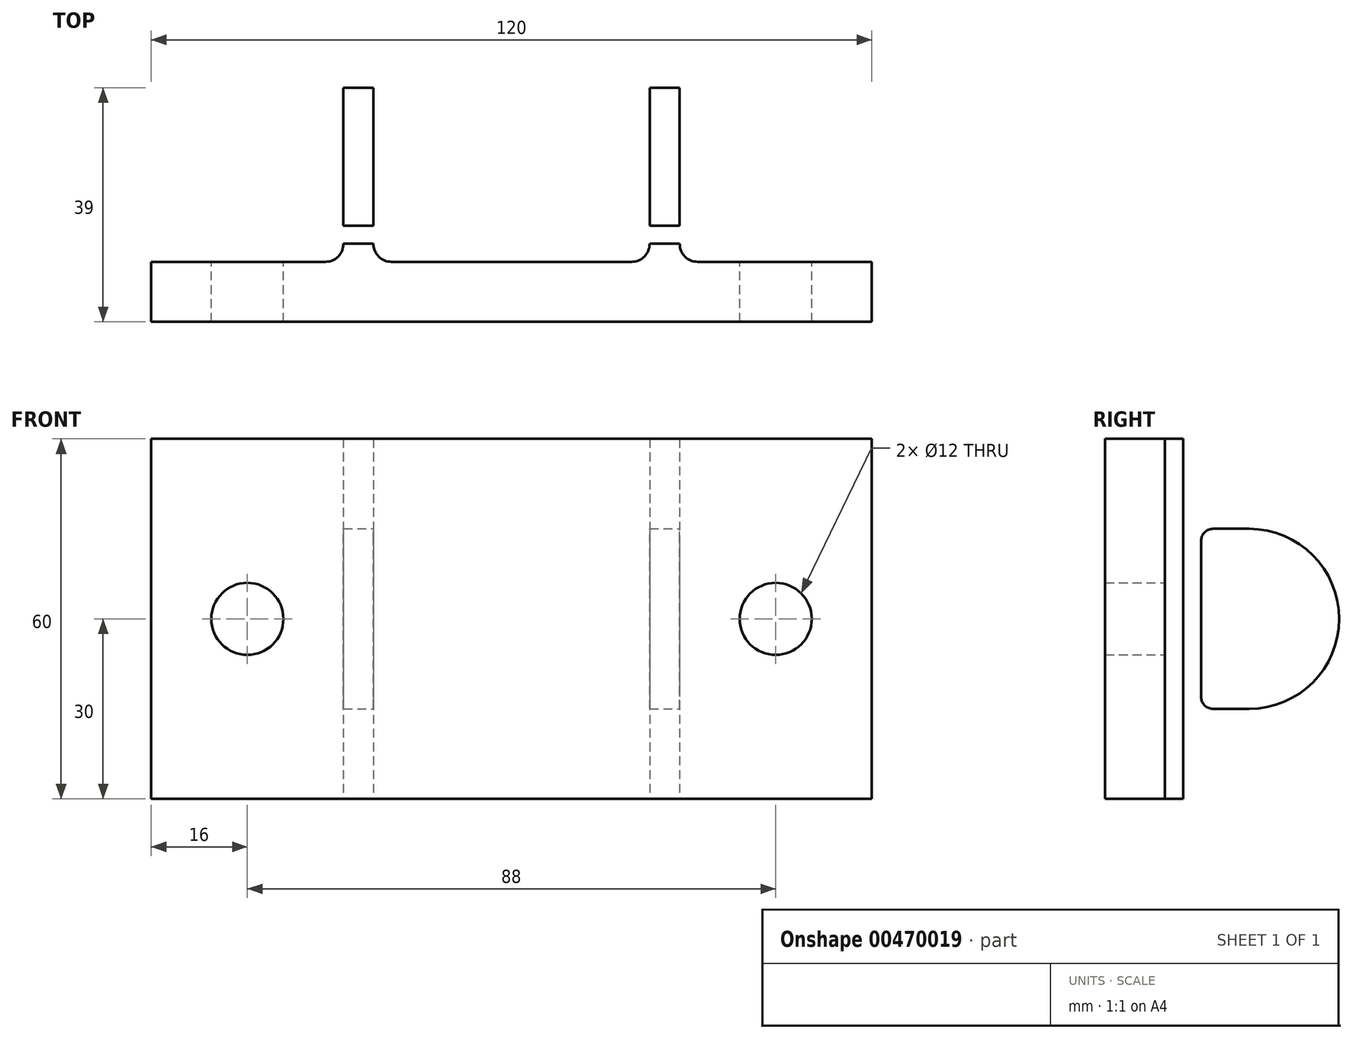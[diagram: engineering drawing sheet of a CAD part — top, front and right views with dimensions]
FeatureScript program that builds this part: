
annotation { "Feature Type Name" : "Feature", "Feature Type Description" : "" }
export const myFeature = defineFeature(function(context is Context, id is Id, definition is map)
    precondition{}
    {
        {
            var Q0;
            Q0=qCreatedBy(makeId("Top.planeOp"),FACE);
            var sketch = newSketch(context, id + "F0", { "sketchPlane" : qUnion([Q0])});
            skLineSegment(sketch, "E0", {"start": v(-60, 0) * mm, "end": v(60, 0) * mm});
            skLineSegment(sketch, "E1", {"start": v(60, 0) * mm, "end": v(60, 10) * mm});
            skLineSegment(sketch, "E2", {"start": v(60, 10) * mm, "end": v(28, 10) * mm});
            skLineSegment(sketch, "E3", {"start": v(28, 10) * mm, "end": v(28, 44) * mm});
            skLineSegment(sketch, "E4", {"start": v(28, 44) * mm, "end": v(23, 44) * mm});
            skLineSegment(sketch, "E5", {"start": v(23, 44) * mm, "end": v(23, 10) * mm});
            skLineSegment(sketch, "E6", {"start": v(23, 10) * mm, "end": v(-23, 10) * mm});
            skLineSegment(sketch, "E7", {"start": v(-23, 10) * mm, "end": v(-23, 44) * mm});
            skLineSegment(sketch, "E8", {"start": v(-23, 44) * mm, "end": v(-28, 44) * mm});
            skLineSegment(sketch, "E9", {"start": v(-28, 44) * mm, "end": v(-28, 10) * mm});
            skLineSegment(sketch, "E10", {"start": v(-28, 10) * mm, "end": v(-60, 10) * mm});
            skLineSegment(sketch, "E11", {"start": v(-60, 10) * mm, "end": v(-60, 0) * mm});
            skSolve(sketch);
        }
        {
            var Q0;
            Q0=qSketchRegion(id+"F0",true);
            extrude(context, id + "F1", {"entities" : qUnion([Q0]), "depth" : 30 * mm, "hasSecondDirection" : true, "secondDirectionOppositeDirection" : true, "secondDirectionDepth" : 30 * mm});
        }
        {
            var Q0;
            Q0=makeQuery(id+"F1.opExtrude","SWEPT_FACE",FACE,{"disambiguationData":[OSD([sQuery(id+"F0.wireOp",EDGE,"E2")])]});
            var sketch = newSketch(context, id + "F2", { "sketchPlane" : qUnion([Q0])});
            skCircle(sketch, "E12", {"center": v(44, 0) * mm, "radius": 6 * mm});
            skPoint(sketch, "E13.center.orphan", {"position": v(-44, 0) * mm});
            skCircle(sketch, "E14", {"center": v(-44, 0) * mm, "radius": 6 * mm});
            skLineSegment(sketch, "E15", {"start": v(28, 0) * mm, "end": v(60, 0) * mm, "construction": true});
            skSolve(sketch);
        }
        {
            var Q0;
            Q0=qSketchRegion(id+"F2",true);
            extrude(context, id + "F3", {"entities" : qUnion([Q0]), "operationType" : NewBodyOperationType.REMOVE, "endBound" : BoundingType.THROUGH_ALL, "oppositeDirection" : true, "depth" : 25 * mm});
        }
        {
            var Q0;
            Q0=makeQuery(id+"F1.opExtrude","SWEPT_EDGE",EDGE,{"disambiguationData":[OSD([sQuery(id+"F0.wireOp",EDGE,"E2"),sQuery(id+"F0.wireOp",EDGE,"E3")])]});
            var Q1;
            Q1=makeQuery(id+"F1.opExtrude","SWEPT_EDGE",EDGE,{"disambiguationData":[OSD([sQuery(id+"F0.wireOp",EDGE,"E5"),sQuery(id+"F0.wireOp",EDGE,"E6")])]});
            var Q2;
            Q2=makeQuery(id+"F1.opExtrude","SWEPT_EDGE",EDGE,{"disambiguationData":[OSD([sQuery(id+"F0.wireOp",EDGE,"E9"),sQuery(id+"F0.wireOp",EDGE,"E10")])]});
            var Q3;
            Q3=makeQuery(id+"F1.opExtrude","SWEPT_EDGE",EDGE,{"disambiguationData":[OSD([sQuery(id+"F0.wireOp",EDGE,"E6"),sQuery(id+"F0.wireOp",EDGE,"E7")])]});
            fillet(context, id + "F4", {"entities" : qUnion([Q0, Q1, Q2, Q3]), "radius" : 3 * mm, "tangentPropagation" : true, "allowEdgeOverflow" : false});
        }
        {
            var Q0;
            Q0=makeQuery(id+"F1.opExtrude","SWEPT_FACE",FACE,{"disambiguationData":[OSD([sQuery(id+"F0.wireOp",EDGE,"E3")])]});
            var sketch = newSketch(context, id + "F5", { "sketchPlane" : qUnion([Q0])});
            skArc(sketch, "E16.0.startCap", {"start": v(24, 15) * mm, "mid": v(39, 0) * mm, "end": v(24, -15) * mm});
            skLineSegment(sketch, "E17", {"start": v(24, 15) * mm, "end": v(16, 15) * mm});
            skLineSegment(sketch, "E18.bottom", {"start": v(16, 15) * mm, "end": v(24, 15) * mm});
            skLineSegment(sketch, "E18.top", {"start": v(16, -15) * mm, "end": v(24, -15) * mm});
            skLineSegment(sketch, "E18.left", {"start": v(16, 15) * mm, "end": v(16, -15) * mm});
            skLineSegment(sketch, "E18.right", {"start": v(24, 15) * mm, "end": v(24, -15) * mm});
            skSolve(sketch);
        }
        {
            var Q0;
            Q0=makeQuery(id+"F5.imprint","IMPRINT",FACE,{"disambiguationData":[TD([[makeQuery(id+"F5.imprint","IMPRINT",EDGE,{"derivedFrom":sQuery(id+"F5.wireOp",EDGE,"E16.0.startCap")}),-1.0]])]});
            var Q1;
            Q1=makeQuery(id+"F5.imprint","IMPRINT",FACE,{"disambiguationData":[TD([[makeQuery(id+"F5.imprint","IMPRINT",EDGE,{"derivedFrom":sQuery(id+"F5.wireOp",EDGE,"E18.bottom")}),-1.0]])]});
            extrude(context, id + "F6", {"entities" : qUnion([Q0, Q1]), "operationType" : NewBodyOperationType.REMOVE, "oppositeDirection" : true, "depth" : 100 * mm, "offsetDistance" : 25 * mm});
        }
        {
            var Q0;
            {var subQ0=sQuery(id+"F5.wireOp",EDGE,"E18.top");var subQ1=sQuery(id+"F5.wireOp",EDGE,"E18.left");Q0=makeQuery(id+"F6.boolean.opBoolean","COPY",EDGE,{"disambiguationData":[TD([makeQuery(id+"F1.opExtrude","SWEPT_FACE",FACE,{"disambiguationData":[OSD([sQuery(id+"F0.wireOp",EDGE,"E3")])]})])],"derivedFrom":makeQuery(id+"F6.opExtrude","SWEPT_EDGE",EDGE,{"disambiguationData":[OSD([subQ0,subQ1])]})});}
            var Q1;
            {var subQ0=sQuery(id+"F5.wireOp",EDGE,"E18.left");var subQ1=sQuery(id+"F5.wireOp",EDGE,"E18.top");Q1=makeQuery(id+"F6.boolean.opBoolean","COPY",EDGE,{"disambiguationData":[TD([makeQuery(id+"F1.opExtrude","SWEPT_FACE",FACE,{"disambiguationData":[OSD([sQuery(id+"F0.wireOp",EDGE,"E7")])]})])],"derivedFrom":makeQuery(id+"F6.opExtrude","SWEPT_EDGE",EDGE,{"disambiguationData":[OSD([subQ1,subQ0])]})});}
            var Q2;
            {var subQ0=sQuery(id+"F5.wireOp",EDGE,"E18.bottom");var subQ1=sQuery(id+"F5.wireOp",EDGE,"E18.left");Q2=makeQuery(id+"F6.boolean.opBoolean","COPY",EDGE,{"disambiguationData":[TD([makeQuery(id+"F1.opExtrude","SWEPT_FACE",FACE,{"disambiguationData":[OSD([sQuery(id+"F0.wireOp",EDGE,"E3")])]})])],"derivedFrom":makeQuery(id+"F6.opExtrude","SWEPT_EDGE",EDGE,{"disambiguationData":[OSD([subQ0,subQ1])]})});}
            var Q3;
            {var subQ0=sQuery(id+"F5.wireOp",EDGE,"E18.left");var subQ1=sQuery(id+"F5.wireOp",EDGE,"E18.bottom");Q3=makeQuery(id+"F6.boolean.opBoolean","COPY",EDGE,{"disambiguationData":[TD([makeQuery(id+"F1.opExtrude","SWEPT_FACE",FACE,{"disambiguationData":[OSD([sQuery(id+"F0.wireOp",EDGE,"E7")])]})])],"derivedFrom":makeQuery(id+"F6.opExtrude","SWEPT_EDGE",EDGE,{"disambiguationData":[OSD([subQ1,subQ0])]})});}
            fillet(context, id + "F7", {"entities" : qUnion([Q0, Q1, Q2, Q3]), "radius" : 2 * mm, "tangentPropagation" : true, "allowEdgeOverflow" : false});
        }
    });
